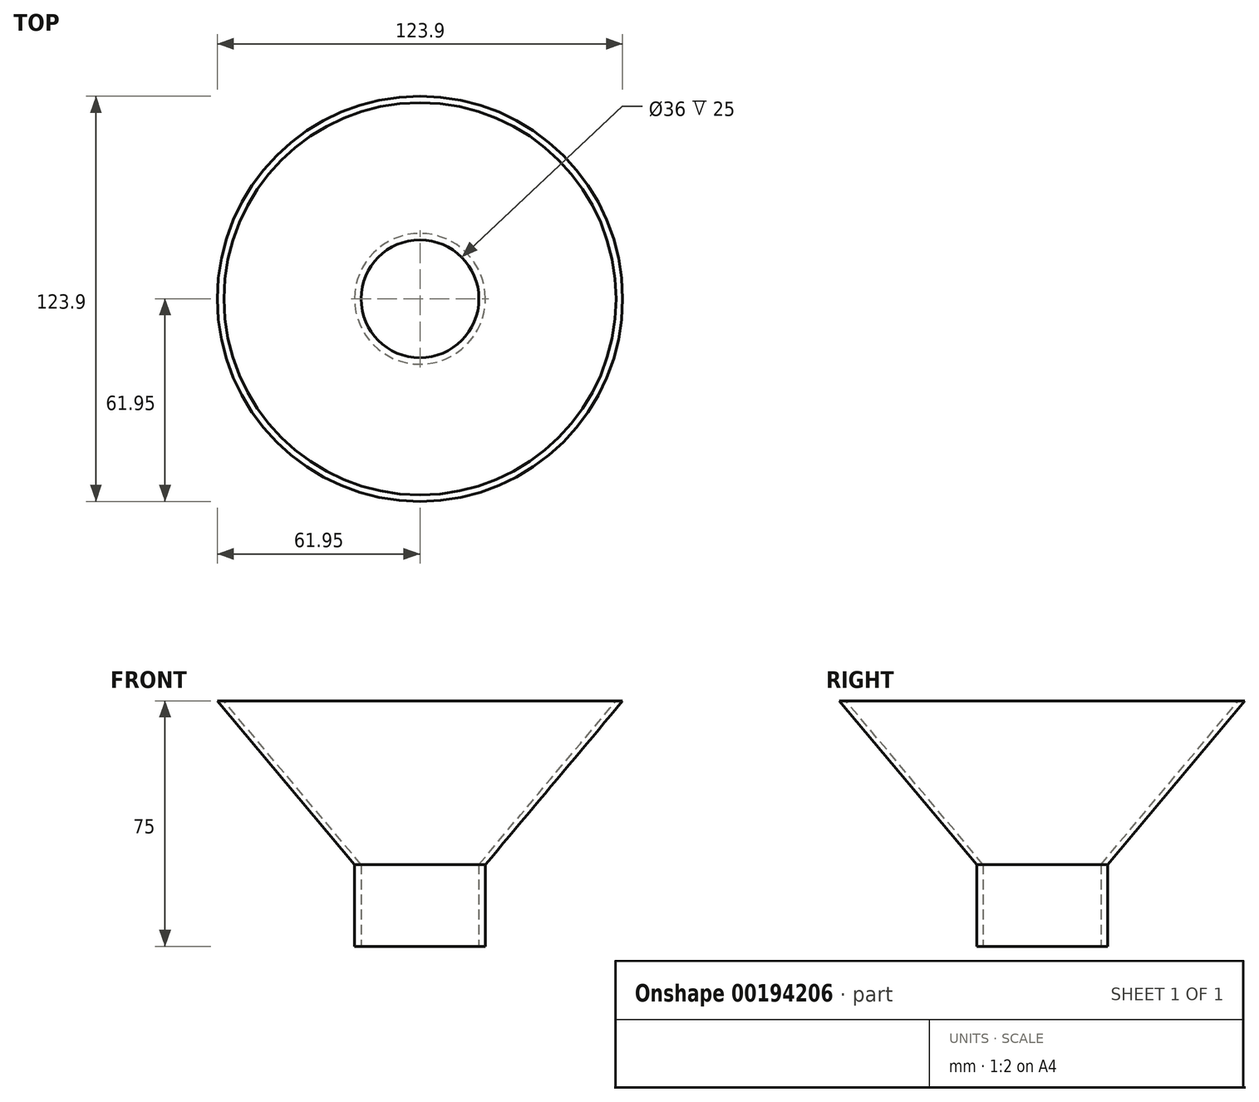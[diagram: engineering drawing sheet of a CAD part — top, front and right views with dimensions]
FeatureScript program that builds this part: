
annotation { "Feature Type Name" : "Feature", "Feature Type Description" : "" }
export const myFeature = defineFeature(function(context is Context, id is Id, definition is map)
    precondition{}
    {
        {
            var Q0;
            Q0=qCreatedBy(makeId("Top.planeOp"),FACE);
            var sketch = newSketch(context, id + "F0", { "sketchPlane" : qUnion([Q0])});
            skCircle(sketch, "E0", {"center": v(0, 0) * mm, "radius": 18 * mm});
            skCircle(sketch, "E1.0", {"center": v(0, 0) * mm, "radius": 20 * mm});
            skSolve(sketch);
        }
        {
            var Q0;
            Q0=makeQuery(id+"F0.imprint","IMPRINT",FACE,{"disambiguationData":[TD([[makeQuery(id+"F0.imprint","IMPRINT",EDGE,{"derivedFrom":sQuery(id+"F0.wireOp",EDGE,"E0")}),-1.0]])]});
            extrude(context, id + "F1", {"entities" : qUnion([Q0]), "depth" : 25 * mm});
        }
        {
            var Q0;
            Q0=makeQuery(id+"F1.opExtrude","CAP_FACE",FACE,{"disambiguationData":[OSD([sQuery(id+"F0.wireOp",EDGE,"E0"),sQuery(id+"F0.wireOp",EDGE,"E1.0")])],"isStart":false});
            var sketch = newSketch(context, id + "F2", { "sketchPlane" : qUnion([Q0])});
            skSolve(sketch);
        }
        {
            var Q0;
            Q0=makeQuery(id+"F2.imprint","IMPRINT",FACE,{"disambiguationData":[TD([[makeQuery(id+"F2.imprint","IMPRINT",EDGE,{"derivedFrom":makeQuery(id+"F1.opExtrude","CAP_EDGE",EDGE,{"disambiguationData":[OSD([sQuery(id+"F0.wireOp",EDGE,"E0")])],"isStart":false})}),-1.0]])]});
            extrude(context, id + "F3", {"entities" : qUnion([Q0]), "operationType" : NewBodyOperationType.ADD, "depth" : 50 * mm, "hasDraft" : true, "draftAngle" : 40 * degree, "hasSecondDirectionDraft" : true, "secondDirectionDraftAngle" : 40 * degree});
        }
        {
            var Q0;
            Q0=makeQuery(id+"F2.imprint","IMPRINT",FACE,{"disambiguationData":[TD([[makeQuery(id+"F2.imprint","IMPRINT",EDGE,{"derivedFrom":makeQuery(id+"F1.opExtrude","CAP_EDGE",EDGE,{"disambiguationData":[OSD([sQuery(id+"F0.wireOp",EDGE,"E0")])],"isStart":false})}),1.0]])]});
            extrude(context, id + "F4", {"entities" : qUnion([Q0]), "operationType" : NewBodyOperationType.REMOVE, "depth" : 50 * mm, "hasDraft" : true, "draftAngle" : 40 * degree});
        }
    });
